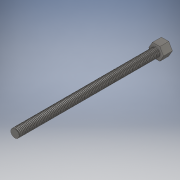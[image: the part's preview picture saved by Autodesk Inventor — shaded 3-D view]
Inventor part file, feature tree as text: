
AUTODESK INVENTOR PART (.ipt)
format: ipt  version: 2019 (Build 230136000, 136)  size: 858,112 bytes
history: native  units: mm
features: sketch x3, extrude x2, helix x1
ambient origin geometry x8: Origin, YZ Plane, XZ Plane, XY Plane, X Axis, Y Axis, Z Axis, Center Point
bodies: Solid1 (feature_tree)
feature tree (6):
  extrude  "Extrusion1"  Depth=118.75mm TaperAngle=0.0deg
  extrude  "Extrusion2"  Depth=5.369358mm
  helix  "Coil1"  [1 undecoded]
  sketch  "Sketch1"  dims[d0=7.0mm d1=118.75mm d2=0.0mm]
  sketch  "Sketch2"  dims[d3=12.4mm d4=5.369358mm d5=7.5mm d6=0.0mm]
  sketch  "Sketch3"  dims[d7=0.5mm d8=0.5mm d9=10.0mm d10=118.75mm d11=1000.0mm d12=0.0mm d13=90.0deg d14=90.0deg d15=0.0mm d16=0.0mm]
note: 1 required parameter value undecoded (feature->parameter linkage not recoverable at this tier; creation-order binding heuristic only, values carry confidence <= 0.55)
